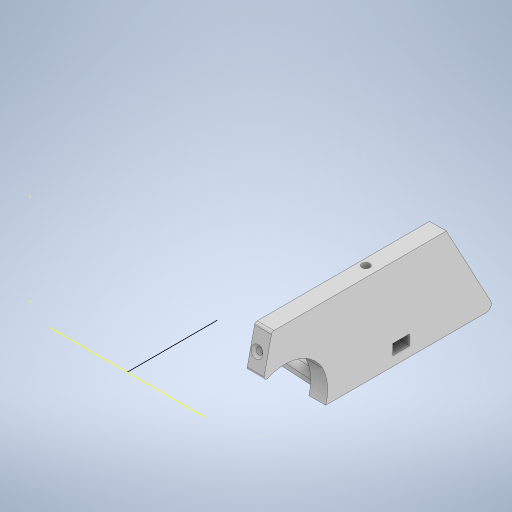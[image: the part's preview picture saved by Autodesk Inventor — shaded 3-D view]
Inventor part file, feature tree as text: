
AUTODESK INVENTOR PART (.ipt)
format: ipt  version: 2023 (Build 270158000, 158)  size: 2,942,464 bytes
history: native  units: mm
features: projected_geometry x146, extrude x135, sketch x101, fillet x14, reference x6, other x5, plane x3, mirror x3, chamfer x2
ambient origin geometry x8: Origin, YZ Plane, XZ Plane, XY Plane, X Axis, Y Axis, Z Axis, Center Point
bodies: Solid1 (feature_tree)
feature tree (415):
  sketch  "Sketch1"  dims[d0=100.0mm d1=100.0mm]
  extrude  "Extrusion1"  Depth=100.0mm
  extrude  "Extrusion2"  Depth=20.0mm
  extrude  "Extrusion3"  Depth=20.0mm
  sketch  "Sketch3"  dims[d4=31.0mm d5=20.0mm]
  extrude  "Extrusion4"  Depth=19.0mm
  extrude  "Extrusion5"  Depth=10.0mm
  sketch  "Sketch4"  dims[d6=14.0mm d7=19.0mm]
  plane  "Work Plane1"
  mirror  "Mirror1"
  extrude  "Extrusion6"  Depth=10.0mm
  sketch  "Sketch8"  dims[d10=10.0mm d11=2.0mm]
  extrude  "Extrusion7"  Depth=15.0mm
  extrude  "Extrusion8"  Depth=2.0mm
  extrude  "Extrusion9"  Depth=1.0mm
  sketch  "Sketch9"  dims[d12=2.0mm d13=15.0mm]
  extrude  "Extrusion10"  Depth=10.0mm TaperAngle=0.0deg
  extrude  "Extrusion11"  TaperAngle=0.0deg  [1 undecoded]
  sketch  "Sketch10"  dims[d14=15.0mm d15=2.0mm]
  extrude  "Extrusion12"  Depth=14.0mm TaperAngle=0.0deg
  extrude  "Extrusion13"  TaperAngle=90.0deg  [1 undecoded]
  extrude  "Extrusion14"  Depth=40.0mm
  sketch  "Sketch12"  dims[d18=10.0mm d19=0.0mm d20=2.0mm d21=0.0mm]
  extrude  "Extrusion15"  Depth=25.0mm
  extrude  "Extrusion16"  Depth=5.0mm
  extrude  "Extrusion17"  Depth=13.0mm
  extrude  "Extrusion18"  Depth=8.0mm
  extrude  "Extrusion19"  Depth=18.0mm TaperAngle=0.0deg
  extrude  "Extrusion20"  Depth=49.0mm
  extrude  "Extrusion21"  Depth=5.0mm
  sketch  "Sketch15"  dims[d28=14.25mm d29=0.0mm d30=90.0deg]
  plane  "Work Plane2"
  mirror  "Mirror2"
  extrude  "Extrusion22"  TaperAngle=0.0deg  [1 undecoded]
  sketch  "Sketch17"  dims[d36=15.0mm d37=25.0mm]
  extrude  "Extrusion23"  Depth=10.0mm
  extrude  "Extrusion24"  Depth=1.6mm
  extrude  "Extrusion25"  TaperAngle=0.0deg  [1 undecoded]
  extrude  "Extrusion26"  Depth=14.0mm TaperAngle=0.0deg
  extrude  "Extrusion27"  Depth=6.0mm
  sketch  "Sketch21"  dims[d44=18.0mm d45=0.0mm d46=18.0mm d47=0.0mm]
  extrude  "Extrusion28"  Depth=2.0mm
  extrude  "Extrusion29"  Depth=6.0mm TaperAngle=0.0deg
  sketch  "Sketch22"  dims[d48=0.0mm d49=0.0mm d50=49.0mm]
  extrude  "Extrusion30"  Depth=15.0mm TaperAngle=0.0deg
  extrude  "Extrusion31"  Depth=3.2mm
  extrude  "Extrusion32"  Depth=4.0mm
  extrude  "Extrusion33"  Depth=1.0mm TaperAngle=0.0deg
  extrude  "Extrusion34"  Depth=3.0mm
  extrude  "Extrusion35"  Depth=15.0mm TaperAngle=0.0deg
  extrude  "Extrusion36"  Depth=3.2mm
  fillet  "Face Fillet1"
  fillet  "Face Fillet2"
  extrude  "Extrusion37"  Depth=3.2mm
  fillet  "Face Fillet3"
  fillet  "Face Fillet5"
  extrude  "Extrusion38"  Depth=5.0mm TaperAngle=0.0deg
  extrude  "Extrusion39"  TaperAngle=0.0deg  [1 undecoded]
  fillet  "Fillet2"  Radius=2.8mm
  extrude  "Extrusion40"  Depth=100.0mm TaperAngle=0.0deg
  sketch  "Sketch32"  dims[d76=6.0mm d77=0.0mm d78=15.0mm d79=0.0mm]
  extrude  "Extrusion41"  Depth=11.0mm
  extrude  "Extrusion42"  Depth=9.0mm TaperAngle=0.0deg
  extrude  "Extrusion43"  Depth=3.2mm
  sketch  "Sketch33"  dims[d80=15.0mm d81=0.0mm d82=3.2mm]
  extrude  "Extrusion44"  Depth=7.0mm TaperAngle=0.0deg
  extrude  "Extrusion45"  Depth=40.656mm TaperAngle=0.0deg
  extrude  "Extrusion46"  Depth=9.0mm TaperAngle=0.0deg
  extrude  "Extrusion47"  Depth=3.0mm
  sketch  "Sketch36"  dims[d91=90.0deg d92=3.0mm]
  extrude  "Extrusion48"  Depth=1.5mm TaperAngle=0.0deg
  extrude  "Extrusion49"  Depth=6.0mm
  sketch  "Sketch37"  dims[d93=3.0mm d94=15.0mm d95=0.0mm]
  extrude  "Extrusion50"  Depth=10.0mm TaperAngle=0.0deg
  extrude  "Extrusion51"  Depth=4.0mm
  extrude  "Extrusion52"  Depth=10.0mm TaperAngle=0.0deg
  extrude  "Extrusion53"  Depth=20.0mm TaperAngle=0.0deg
  sketch  "Sketch40"  dims[d100=4.0mm d101=5.0mm d102=0.0mm]
  extrude  "Extrusion54"  Depth=1.5mm
  extrude  "Extrusion55"  Depth=3.0mm
  extrude  "Extrusion56"  Depth=6.4mm
  extrude  "Extrusion57"  Depth=3.0mm
  fillet  "Fillet3"  Radius=2.0mm
  extrude  "Extrusion58"  TaperAngle=0.0deg  [1 undecoded]
  sketch  "Sketch44"  dims[d114=3.4mm d115=9.0mm d116=0.0mm]
  extrude  "Extrusion59"  TaperAngle=0.0deg  [1 undecoded]
  extrude  "Extrusion60"  Depth=10.0mm TaperAngle=0.0deg
  sketch  "Sketch45"  dims[d117=15.0mm d118=0.0mm d119=3.2mm]
  extrude  "Extrusion61"  Depth=10.0mm TaperAngle=0.0deg
  extrude  "Extrusion62"  Depth=3.0mm
  sketch  "Sketch46"  dims[d120=3.2mm d121=7.0mm d122=0.0mm]
  extrude  "Extrusion63"  Depth=6.5mm TaperAngle=0.0deg
  extrude  "Extrusion64"  Depth=17.0mm TaperAngle=0.0deg
  extrude  "Extrusion65"  Depth=3.0mm
  extrude  "Extrusion66"  Depth=5.0mm TaperAngle=0.0deg
  sketch  "Sketch49"  dims[d138=28.734mm d139=3.0mm]
  extrude  "Extrusion67"  Depth=6.5mm TaperAngle=0.0deg
  extrude  "Extrusion68"  Depth=14.0mm TaperAngle=0.0deg
  extrude  "Extrusion69"  Depth=2.0mm
  extrude  "Extrusion70"  Depth=16.0mm TaperAngle=0.0deg
  extrude  "Extrusion71"  Depth=17.0mm TaperAngle=0.0deg
  extrude  "Extrusion72"  Depth=2.5mm
  extrude  "Extrusion73"  Depth=2.0mm
  extrude  "Extrusion74"  TaperAngle=0.0deg  [1 undecoded]
  extrude  "Extrusion75"  Depth=3.0mm TaperAngle=0.0deg
  extrude  "Extrusion76"  Depth=1.0mm
  sketch  "Sketch53"  dims[d149=6.7mm d152=4.0mm]
  extrude  "Extrusion77"  Depth=1.0mm
  extrude  "Extrusion78"  Depth=3.0mm
  extrude  "Extrusion79"  Depth=15.0mm TaperAngle=0.0deg
  extrude  "Extrusion80"  Depth=10.0mm TaperAngle=0.0deg
  extrude  "Extrusion81"  Depth=10.0mm TaperAngle=0.0deg
  extrude  "Extrusion82"  Depth=4.0mm TaperAngle=0.0deg
  extrude  "Extrusion83"  Depth=10.0mm TaperAngle=0.0deg
  sketch  "Sketch59"  dims[d166=6.4mm d167=3.0mm d169=2.0mm]
  extrude  "Extrusion84"  Depth=7.0mm
  extrude  "Extrusion85"  Depth=3.0mm TaperAngle=0.0deg
  extrude  "Extrusion86"  Depth=4.0mm TaperAngle=0.0deg
  extrude  "Extrusion87"  Depth=1.0mm
  extrude  "Extrusion88"  Depth=10.0mm
  sketch  "Sketch62"  dims[d178=10.0mm d179=0.0mm d180=4.0mm d181=0.0mm]
  extrude  "Extrusion89"  Depth=30.0mm TaperAngle=0.0deg
  extrude  "Extrusion90"  Depth=2.5mm
  fillet  "Fillet4"  Radius=11.0mm
  extrude  "Extrusion91"  TaperAngle=0.0deg  [1 undecoded]
  extrude  "Extrusion92"  Depth=10.0mm
  extrude  "Extrusion93"  Depth=3.0mm
  extrude  "Extrusion94"  Depth=1.0mm TaperAngle=0.0deg
  extrude  "Extrusion95"  Depth=5.928mm TaperAngle=0.0deg
  sketch  "Sketch68"  dims[d205=4.0mm d206=0.0mm d207=5.0mm d208=0.0mm]
  extrude  "Extrusion96"  Depth=10.0mm TaperAngle=0.0deg
  extrude  "Extrusion97"  Depth=10.0mm TaperAngle=0.0deg
  extrude  "Extrusion98"  Depth=10.0mm
  extrude  "Extrusion99"  Depth=10.0mm TaperAngle=0.0deg
  extrude  "Extrusion100"  Depth=10.0mm TaperAngle=0.0deg
  sketch  "Sketch74"  dims[d219=6.5mm d220=0.0mm d221=16.0mm d222=0.0mm]
  extrude  "Extrusion101"  Depth=10.0mm TaperAngle=0.0deg
  extrude  "Extrusion102"  Depth=10.0mm
  extrude  "Extrusion103"  Depth=10.0mm TaperAngle=0.0deg
  extrude  "Extrusion104"  Depth=10.0mm TaperAngle=0.0deg
  extrude  "Extrusion105"  Depth=10.0mm
  fillet  "Fillet6"  Radius=1.5mm
  fillet  "Fillet7"  Radius=3.5mm
  extrude  "Extrusion106"  Depth=10.0mm
  fillet  "Fillet8"  Radius=6.5mm
  extrude  "Extrusion107"  Depth=10.0mm TaperAngle=0.0deg
  sketch  "Sketch80"  dims[d239=1.0mm d240=2.5mm]
  extrude  "Extrusion108"  Depth=10.0mm
  extrude  "Extrusion109"  Depth=10.0mm TaperAngle=0.0deg
  extrude  "Extrusion110"  Depth=10.0mm TaperAngle=0.0deg
  extrude  "Extrusion111"  Depth=10.0mm
  extrude  "Extrusion112"  TaperAngle=90.0deg  [1 undecoded]
  fillet  "Fillet9"  Radius=2.7mm
  extrude  "Extrusion113"  Depth=10.0mm TaperAngle=0.0deg
  extrude  "Extrusion114"  Depth=10.0mm
  extrude  "Extrusion115"  Depth=10.0mm TaperAngle=0.0deg
  plane  "Work Plane3"
  mirror  "Mirror3"
  extrude  "Extrusion116"  Depth=10.0mm TaperAngle=0.0deg
  extrude  "Extrusion117"  Depth=10.0mm TaperAngle=0.0deg
  sketch  "Sketch89"  dims[d269=6.5mm d270=0.0mm d271=3.0mm d272=0.0mm]
  extrude  "Extrusion118"  Depth=10.0mm TaperAngle=0.0deg
  extrude  "Extrusion119"  Depth=10.0mm TaperAngle=0.0deg
  extrude  "Extrusion120"  Depth=1.0mm
  chamfer  "Chamfer1"  Distance=1.0mm
  sketch  "Sketch93"  dims[d282=45.0mm d283=30.0mm d284=0.0mm]
  extrude  "Extrusion121"  Depth=10.0mm TaperAngle=0.0deg
  extrude  "Extrusion122"  Depth=1.0mm
  extrude  "Extrusion123"  Depth=10.0mm
  extrude  "Extrusion124"  Depth=10.0mm TaperAngle=0.0deg
  extrude  "Extrusion125"  Depth=10.0mm TaperAngle=0.0deg
  extrude  "Extrusion126"  Depth=10.0mm TaperAngle=0.0deg
  extrude  "Extrusion127"  Depth=10.0mm TaperAngle=0.0deg
  fillet  "Fillet10"  Radius=6.5mm
  extrude  "Extrusion128"  Depth=10.0mm TaperAngle=0.0deg
  extrude  "Extrusion129"  Depth=1.0mm
  extrude  "Extrusion130"  Depth=10.0mm
  fillet  "Fillet11"  Radius=10.0mm
  fillet  "Fillet12"  Radius=15.0mm
  chamfer  "Chamfer2"  Distance=12.0mm
  extrude  "Wyciągnięcie proste131"  Depth=10.0mm
  extrude  "Wyciągnięcie proste132"  Depth=10.0mm
  extrude  "Wyciągnięcie proste133"  Depth=10.0mm
  extrude  "Wyciągnięcie proste134"  Depth=10.0mm TaperAngle=0.0deg
  extrude  "Wyciągnięcie proste135"  Depth=10.0mm TaperAngle=0.0deg
  sketch  "Sketch2"  dims[d2=5.0mm d3=20.0mm]
  projected_geometry  "Projected Loop1"
  sketch  "Sketch6"  dims[d8=10.0mm d9=14.0mm]
  projected_geometry  "Projected Loop5"
  projected_geometry  "Projected Loop6"
  projected_geometry  "Projected Loop7"
  projected_geometry  "Projected Loop8"
  projected_geometry  "Projected Loop9"
  projected_geometry  "Projected Loop10"
  sketch  "Sketch11"  dims[d16=1.0mm d17=5.0mm]
  projected_geometry  "Projected Loop11"
  projected_geometry  "Projected Loop12"
  sketch  "Sketch13"  dims[d22=31.0mm d23=0.0mm d24=0.0mm]
  projected_geometry  "Projected Loop13"
  projected_geometry  "Projected Loop14"
  sketch  "Sketch14"  dims[d25=30.4mm d26=14.0mm d27=0.0mm]
  projected_geometry  "Projected Loop15"
  projected_geometry  "Projected Loop16"
  sketch  "Sketch16"  dims[d33=25.0mm d34=0.0mm d35=40.0mm]
  projected_geometry  "Projected Loop17"
  projected_geometry  "Projected Loop18"
  projected_geometry  "Projected Loop19"
  sketch  "Sketch18"  dims[d38=20.0mm d39=5.0mm]
  projected_geometry  "Projected Loop20"
  projected_geometry  "Projected Loop21"
  projected_geometry  "Projected Loop22"
  projected_geometry  "Projected Loop23"
  projected_geometry  "Projected Loop24"
  projected_geometry  "Projected Loop25"
  projected_geometry  "Projected Loop26"
  sketch  "Sketch19"  dims[d40=7.0mm d41=13.0mm]
  projected_geometry  "Projected Loop27"
  sketch  "Sketch20"  dims[d42=7.0mm d43=8.0mm]
  projected_geometry  "Projected Loop28"
  projected_geometry  "Projected Loop29"
  projected_geometry  "Projected Loop30"
  sketch  "Sketch23"  dims[d51=25.0mm d52=5.0mm]
  sketch  "Sketch24"  dims[d53=20.0mm d54=0.0mm d55=0.0mm]
  projected_geometry  "Projected Loop31"
  projected_geometry  "Projected Loop32"
  sketch  "Sketch25"  dims[d56=10.0mm d57=0.0mm d58=1.6mm]
  projected_geometry  "Projected Loop33"
  sketch  "Sketch26"  dims[d59=1.6mm d60=1.6mm]
  projected_geometry  "Projected Loop34"
  sketch  "Sketch27"  dims[d61=5.0mm d62=0.0mm d63=0.0mm d64=0.0mm]
  projected_geometry  "Projected Loop35"
  sketch  "Sketch28"  dims[d65=2.5mm d66=14.0mm d67=0.0mm]
  projected_geometry  "Projected Loop36"
  sketch  "Sketch29"  dims[d68=2.0mm d69=6.0mm]
  sketch  "Sketch30"  dims[d70=5.0mm d71=2.0mm]
  projected_geometry  "Projected Loop37"
  projected_geometry  "Projected Loop38"
  projected_geometry  "Projected Loop39"
  sketch  "Sketch31"  dims[d72=14.0mm d73=0.0mm d74=6.0mm d75=0.0mm]
  projected_geometry  "Projected Loop40"
  projected_geometry  "Projected Loop41"
  projected_geometry  "Projected Loop42"
  projected_geometry  "Projected Loop43"
  projected_geometry  "Projected Loop44"
  projected_geometry  "Projected Loop45"
  projected_geometry  "Projected Loop46"
  sketch  "Sketch34"  dims[d83=3.2mm d84=4.0mm]
  projected_geometry  "Projected Loop47"
  projected_geometry  "Projected Loop48"
  sketch  "Sketch35"  dims[d85=15.0mm d86=0.0mm d87=1.0mm d88=0.0mm]
  projected_geometry  "Projected Loop49"
  projected_geometry  "Projected Loop50"
  projected_geometry  "Projected Loop51"
  projected_geometry  "Projected Loop52"
  projected_geometry  "Projected Loop53"
  sketch  "Sketch38"  dims[d96=3.2mm d97=3.2mm]
  projected_geometry  "Projected Loop54"
  projected_geometry  "Projected Loop55"
  sketch  "Sketch39"  dims[d98=3.2mm d99=3.2mm]
  projected_geometry  "Projected Loop56"
  sketch  "Sketch41"  dims[d103=5.0mm d104=0.0mm d105=0.0mm d106=0.0mm d107=2.8mm]
  projected_geometry  "Projected Loop57"
  sketch  "Sketch42"  dims[d108=2.8mm d109=100.0mm d110=0.0mm]
  projected_geometry  "Projected Loop58"
  sketch  "Sketch43"  dims[d111=20.0mm d112=0.0mm d113=11.0mm]
  projected_geometry  "Projected Loop59"
  projected_geometry  "Projected Loop60"
  projected_geometry  "Projected Loop61"
  projected_geometry  "Projected Loop62"
  projected_geometry  "Projected Loop63"
  projected_geometry  "Projected Loop64"
  projected_geometry  "Projected Loop65"
  projected_geometry  "Projected Loop66"
  projected_geometry  "Projected Loop67"
  projected_geometry  "Projected Loop68"
  projected_geometry  "Projected Loop69"
  projected_geometry  "Projected Loop70"
  projected_geometry  "Projected Loop71"
  projected_geometry  "Projected Loop72"
  projected_geometry  "Projected Loop73"
  projected_geometry  "Projected Loop74"
  projected_geometry  "Projected Loop75"
  projected_geometry  "Projected Loop76"
  projected_geometry  "Projected Loop77"
  projected_geometry  "Projected Loop78"
  sketch  "Sketch47"  dims[d123=4.0mm d124=0.0mm d125=40.656mm d126=0.0mm]
  projected_geometry  "Projected Loop79"
  sketch  "Sketch48"  dims[d127=3.0mm d128=0.0mm d129=9.0mm d130=0.0mm]
  projected_geometry  "Projected Loop80"
  projected_geometry  "Projected Loop81"
  sketch  "Sketch50"  dims[d140=1.5mm d141=0.0mm d142=1.5mm d143=0.0mm]
  projected_geometry  "Projected Loop82"
  projected_geometry  "Projected Loop83"
  sketch  "Sketch51"  dims[d144=6.0mm d145=6.0mm]
  projected_geometry  "Projected Loop84"
  sketch  "Sketch52"  dims[d146=2.0mm d147=10.0mm d148=0.0mm]
  projected_geometry  "Projected Loop85"
  projected_geometry  "Projected Loop86"
  projected_geometry  "Projected Loop87"
  sketch  "Sketch54"  dims[d153=10.0mm d154=0.0mm d155=16.0mm d156=0.0mm]
  projected_geometry  "Projected Loop88"
  projected_geometry  "Projected Loop89"
  sketch  "Sketch55"  dims[d157=1e-05mm d158=20.0mm d159=0.0mm]
  projected_geometry  "Projected Loop90"
  projected_geometry  "Projected Loop91"
  sketch  "Sketch56"  dims[d160=6.4mm d161=1.5mm]
  projected_geometry  "Projected Loop92"
  projected_geometry  "Projected Loop93"
  projected_geometry  "Projected Loop94"
  sketch  "Sketch57"  dims[d162=16.5mm d163=3.0mm]
  projected_geometry  "Projected Loop95"
  projected_geometry  "Projected Loop96"
  projected_geometry  "Projected Loop97"
  sketch  "Sketch58"  dims[d164=3.0mm d165=6.4mm]
  projected_geometry  "Projected Loop98"
  projected_geometry  "Projected Loop99"
  projected_geometry  "Projected Loop100"
  projected_geometry  "Projected Loop101"
  sketch  "Sketch60"  dims[d170=5.928mm d171=0.0mm d172=0.0mm d173=0.0mm]
  projected_geometry  "Projected Loop102"
  projected_geometry  "Projected Loop103"
  sketch  "Sketch61"  dims[d174=3.0mm d175=0.0mm d176=0.0mm d177=0.0mm]
  projected_geometry  "Projected Loop104"
  projected_geometry  "Projected Loop105"
  projected_geometry  "Projected Loop106"
  projected_geometry  "Projected Loop107"
  projected_geometry  "Projected Loop108"
  projected_geometry  "Projected Loop109"
  projected_geometry  "Projected Loop110"
  projected_geometry  "Projected Loop111"
  sketch  "Sketch63"  dims[d182=2.5mm d183=10.0mm d184=0.0mm]
  projected_geometry  "Projected Loop112"
  sketch  "Sketch64"  dims[d185=2.0mm d186=3.0mm]
  projected_geometry  "Projected Loop113"
  sketch  "Sketch65"  dims[d195=0.0mm d196=0.0mm d197=6.5mm d198=0.0mm]
  projected_geometry  "Projected Loop114"
  reference  "Reference1"
  sketch  "Sketch66"  dims[d199=2.5mm d200=17.0mm d201=0.0mm]
  reference  "Reference2"
  reference  "Reference3"
  sketch  "Sketch67"  dims[d202=14.0mm d203=0.0mm d204=3.0mm]
  projected_geometry  "Projected Loop115"
  projected_geometry  "Projected Loop116"
  sketch  "Sketch69"  dims[d209=2.5mm d210=6.5mm d211=0.0mm]
  projected_geometry  "Projected Loop117"
  sketch  "Sketch72"  dims[d212=0.0mm d213=0.0mm d214=14.0mm d215=0.0mm]
  projected_geometry  "Projected Loop118"
  sketch  "Sketch73"  dims[d216=6.5mm d217=0.0mm d218=2.0mm]
  projected_geometry  "Projected Loop119"
  projected_geometry  "Projected Loop120"
  sketch  "Sketch75"  dims[d223=17.0mm d224=0.0mm d225=17.0mm d226=0.0mm]
  reference  "Reference4"
  projected_geometry  "Projected Loop121"
  sketch  "Sketch76"  dims[d227=17.0mm d228=0.0mm d229=2.5mm]
  projected_geometry  "Projected Loop122"
  sketch  "Sketch77"  dims[d230=2.5mm d231=2.0mm]
  projected_geometry  "Projected Loop123"
  sketch  "Sketch78"  dims[d232=13.0mm d233=0.0mm d234=0.0mm]
  projected_geometry  "Projected Loop124"
  sketch  "Sketch79"  dims[d235=6.5mm d236=0.0mm d237=3.0mm d238=0.0mm]
  projected_geometry  "Projected Loop125"
  projected_geometry  "Projected Loop126"
  projected_geometry  "Projected Loop127"
  sketch  "Sketch81"  dims[d241=14.0mm d242=0.0mm d243=1.0mm]
  sketch  "Sketch82"  dims[d244=2.0mm d245=3.0mm]
  projected_geometry  "Projected Loop128"
  sketch  "Sketch83"  dims[d246=3.2mm d247=15.0mm d248=0.0mm]
  projected_geometry  "Projected Loop129"
  projected_geometry  "Projected Loop130"
  sketch  "Sketch84"  dims[d249=10.0mm d250=0.0mm d251=10.0mm d252=0.0mm]
  projected_geometry  "Projected Loop131"
  reference  "Reference5"
  projected_geometry  "Projected Loop132"
  sketch  "Sketch85"  dims[d253=3.0mm d254=0.0mm d255=10.0mm d256=0.0mm]
  sketch  "Sketch86"  dims[d257=8.0mm d258=0.0mm d259=4.0mm d260=0.0mm]
  sketch  "Sketch87"  dims[d261=2.5mm d262=10.0mm d263=0.0mm]
  projected_geometry  "Projected Loop133"
  projected_geometry  "Projected Loop134"
  sketch  "Sketch88"  dims[d266=7.0mm d268=7.0mm]
  projected_geometry  "Projected Loop135"
  sketch  "Sketch90"  dims[d273=8.0mm d274=0.0mm d275=4.0mm d276=0.0mm]
  sketch  "Sketch91"  dims[d277=1.0mm d278=1.0mm]
  projected_geometry  "Projected Loop136"
  sketch  "Sketch92"  dims[d279=10.0mm d280=0.0mm d281=1.308997mm]
  projected_geometry  "Projected Loop137"
  projected_geometry  "Projected Loop138"
  sketch  "Sketch94"  dims[d285=2.0mm d286=2.5mm d287=11.0mm d288=0.0mm]
  projected_geometry  "Projected Loop139"
  sketch  "Sketch95"  dims[d289=135.0deg d290=0.0mm d291=0.0mm]
  projected_geometry  "Projected Loop140"
  sketch  "Sketch96"  dims[d292=3.7mm d293=0.0mm d294=10.0mm]
  projected_geometry  "Projected Loop141"
  sketch  "Sketch97"  dims[d295=6.4mm d296=3.0mm]
  projected_geometry  "Projected Loop142"
  reference  "Reference6"
  sketch  "Sketch98"  dims[d297=0.0mm d298=0.0mm d299=1.0mm d300=0.0mm]
  projected_geometry  "Projected Loop143"
  sketch  "Sketch99"  dims[d301=1.5mm d302=0.0mm d303=5.928mm d304=0.0mm]
  projected_geometry  "Projected Loop144"
  sketch  "Sketch100"  dims[d305=12.0mm d306=0.0mm d307=12.0mm d308=0.0mm d309=12.0mm d310=0.0mm d311=2.0mm d312=41.5mm d313=0.0mm d314=5.0mm d315=0.0mm d316=6.5mm d317=0.0mm d318=2.5mm d319=15.0mm d320=0.0mm d321=15.0mm d322=0.0mm d323=6.4mm d324=1.5mm d325=3.5mm d326=3.5mm d327=6.5mm d328=0.0mm d329=6.5mm d330=0.0mm d331=1.047198mm d332=11.908mm d333=0.0mm d334=12.0mm d335=0.0mm d336=8.0mm d337=90.0deg d338=2.7mm d339=10.0mm d340=0.0mm d341=6.4mm d342=10.0mm d343=0.0mm d344=6.5mm d345=0.0mm d346=6.5mm d347=0.0mm d348=6.5mm d349=0.0mm d350=6.5mm d351=0.0mm d353=1.0mm d354=1.0mm d355=6.5mm d356=0.0mm d357=1.0mm d358=2.0mm d359=6.5mm d360=0.0mm d361=4.0mm d362=0.0mm d363=4.0mm d364=0.0mm d365=44.0mm d366=0.0mm d367=6.5mm d368=0.0mm d369=6.5mm d370=0.0mm d371=1.0mm d372=4.0mm d373=10.0mm d374=0.0mm d375=15.0mm d376=0.0mm d377=12.0mm d378=0.0mm d379=41.75mm d380=6.0mm d381=6.0mm d382=6.5mm d383=0.0mm d384=4.0mm d385=0.0mm d386=0.0mm d387=0.0mm d388=1.5mm d389=1.5mm d390=10.0mm d391=0.0mm d392=3.0mm d393=5.0mm d394=0.0mm d395=1.0mm d396=2.0mm d397=45.0deg d398=9.0mm d399=8.0mm d400=0.0mm d401=6.5mm d402=0.0mm d403=6.5mm d404=0.0mm d405=6.5mm d406=0.0mm d407=10.0mm d408=0.0mm d409=6.5mm d410=0.0mm d411=6.5mm d412=0.0mm d413=0.4mm d414=6.5mm d415=0.0mm d416=2.0mm d417=14.0mm d418=0.0mm d419=6.5mm d420=0.0mm d421=0.4mm d422=10.0mm d423=1.0mm d424=2.0mm d425=45.0deg d426=10.0mm d427=0.0mm d428=10.0mm d429=0.0mm d430=10.0mm d431=0.0mm d432=10.0mm d433=0.0mm d434=0.0mm d435=0.0mm d150=0.0mm d151=0.0mm d352=0.0mm]
  projected_geometry  "Projected Loop145"
  sketch  "Szkic101"
  projected_geometry  "Pętla rzutowana146"
  sketch  "Szkic102"
  projected_geometry  "Pętla rzutowana147"
  sketch  "Szkic103"
  sketch  "Szkic104"
  projected_geometry  "Pętla rzutowana148"
  sketch  "Szkic105"
  projected_geometry  "Pętla rzutowana149"
  parser-record x1  (decoder bookkeeping rows leaked as tree rows — omitted from the tree; the rows remain in map.json)
  other  "zlozenie.iam"
  other  "sciana_lewa_v4:1"
  other  "<userpath>\Desktop\MojeRoboty\Stefan\mechanics\zlozenie.iam"
  other  "sciana_lewa_v5:1"
note: 10 required parameter values undecoded (feature->parameter linkage not recoverable at this tier; creation-order binding heuristic only, values carry confidence <= 0.55)
note: 1 file-system path scrubbed to <path> (originals preserved in map.json)
